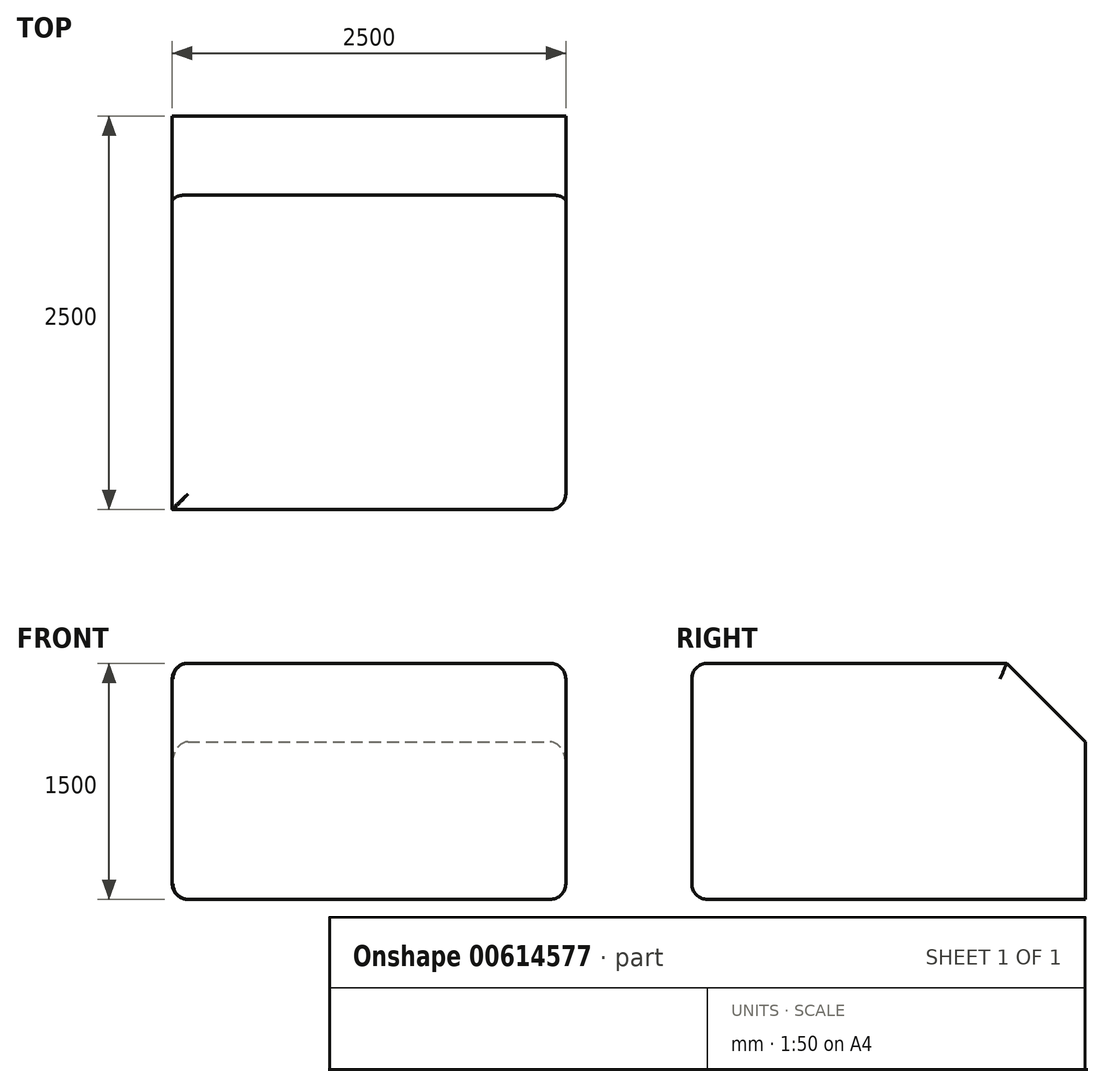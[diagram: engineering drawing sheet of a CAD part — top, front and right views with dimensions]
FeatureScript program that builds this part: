
annotation { "Feature Type Name" : "Feature", "Feature Type Description" : "" }
export const myFeature = defineFeature(function(context is Context, id is Id, definition is map)
    precondition{}
    {
        {
            var Q0;
            Q0=qCreatedBy(makeId("Top.planeOp"),FACE);
            var sketch = newSketch(context, id + "F0", { "sketchPlane" : qUnion([Q0])});
            skLineSegment(sketch, "E0.bottom", {"start": v(1250, -1250) * mm, "end": v(-1245, -1250) * mm});
            skLineSegment(sketch, "E0.top", {"start": v(1250, 1250) * mm, "end": v(-1250, 1250) * mm});
            skLineSegment(sketch, "E0.left", {"start": v(1250, -1250) * mm, "end": v(1250, 1250) * mm});
            skLineSegment(sketch, "E0.right", {"start": v(-1250, -1245) * mm, "end": v(-1250, 1250) * mm});
            skPoint(sketch, "E0.middle", {"position": v(0, 0) * mm});
            skPoint(sketch, "E1.visualSharp", {"position": v(-1250, -1250) * mm});
            skArc(sketch, "E1.filletArc", {"start": v(-1250, -1245) * mm, "mid": v(-1248.54, -1248.54) * mm, "end": v(-1245, -1250) * mm});
            skSolve(sketch);
        }
        {
            var Q0;
            Q0 = qSketchRegion(id + "F0", true);
            var Q1;
            Q1=makeQuery(id+"F0.imprint","IMPRINT",FACE,{"disambiguationData":[TD([[makeQuery(id+"F0.imprint","IMPRINT",EDGE,{"derivedFrom":sQuery(id+"F0.wireOp",EDGE,"E0.bottom")}),-1.0]])]});
            extrude(context, id + "F1", {"entities" : qUnion([Q0, Q1]), "depth" : 1500 * mm, "offsetDistance" : 25 * mm});
        }
        {
            var Q0;
            Q0=makeQuery(id+"F1.opExtrude","CAP_EDGE",EDGE,{"disambiguationData":[OSD([sQuery(id+"F0.wireOp",EDGE,"E0.top")])],"isStart":false});
            chamfer(context, id + "F2", {"entities" : qUnion([Q0]), "width" : 500 * mm, "tangentPropagation" : true});
        }
        {
            var Q0;
            Q0=makeQuery(id+"F1.opExtrude","CAP_EDGE",EDGE,{"disambiguationData":[OSD([sQuery(id+"F0.wireOp",EDGE,"E0.right")])],"isStart":true});
            var Q1;
            Q1=makeQuery(id+"F1.opExtrude","CAP_EDGE",EDGE,{"disambiguationData":[OSD([sQuery(id+"F0.wireOp",EDGE,"E0.left")])],"isStart":true});
            var Q2;
            Q2=makeQuery(id+"F1.opExtrude","SWEPT_EDGE",EDGE,{"disambiguationData":[OSD([sQuery(id+"F0.wireOp",EDGE,"E0.right"),sQuery(id+"F0.wireOp",EDGE,"E1.filletArc")])]});
            var Q3;
            Q3=makeQuery(id+"F1.opExtrude","CAP_EDGE",EDGE,{"disambiguationData":[OSD([sQuery(id+"F0.wireOp",EDGE,"E0.bottom")])],"isStart":false});
            var Q4;
            Q4=makeQuery(id+"F1.opExtrude","SWEPT_EDGE",EDGE,{"disambiguationData":[OSD([sQuery(id+"F0.wireOp",EDGE,"E0.bottom"),sQuery(id+"F0.wireOp",EDGE,"E0.left")])]});
            var Q5;
            Q5=makeQuery(id+"F1.opExtrude","CAP_EDGE",EDGE,{"disambiguationData":[OSD([sQuery(id+"F0.wireOp",EDGE,"E0.bottom")])],"isStart":true});
            var Q6;
            Q6=makeQuery(id+"F1.opExtrude","CAP_EDGE",EDGE,{"disambiguationData":[OSD([sQuery(id+"F0.wireOp",EDGE,"E0.right")])],"isStart":false});
            var Q7;
            Q7=makeQuery(id+"F2.opChamfer","BLEND_EDGE",EDGE,{"blendedFrom":[makeQuery(id+"F1.opExtrude","CAP_EDGE",EDGE,{"disambiguationData":[OSD([sQuery(id+"F0.wireOp",EDGE,"E0.top")])],"isStart":false}),makeQuery(id+"F1.opExtrude","SWEPT_FACE",FACE,{"disambiguationData":[OSD([sQuery(id+"F0.wireOp",EDGE,"E0.right")])]})],"blendedInto":[makeQuery(id+"F1.opExtrude","SWEPT_FACE",FACE,{"disambiguationData":[OSD([sQuery(id+"F0.wireOp",EDGE,"E0.right")])]})]});
            var Q8;
            Q8=makeQuery(id+"F1.opExtrude","CAP_EDGE",EDGE,{"disambiguationData":[OSD([sQuery(id+"F0.wireOp",EDGE,"E0.left")])],"isStart":false});
            var Q9;
            Q9=makeQuery(id+"F2.opChamfer","BLEND_EDGE",EDGE,{"blendedFrom":[makeQuery(id+"F1.opExtrude","CAP_EDGE",EDGE,{"disambiguationData":[OSD([sQuery(id+"F0.wireOp",EDGE,"E0.top")])],"isStart":false}),makeQuery(id+"F1.opExtrude","SWEPT_FACE",FACE,{"disambiguationData":[OSD([sQuery(id+"F0.wireOp",EDGE,"E0.left")])]})],"blendedInto":[makeQuery(id+"F1.opExtrude","SWEPT_FACE",FACE,{"disambiguationData":[OSD([sQuery(id+"F0.wireOp",EDGE,"E0.left")])]})]});
            fillet(context, id + "F3", {"entities" : qUnion([Q0, Q1, Q2, Q3, Q4, Q5, Q6, Q7, Q8, Q9]), "radius" : 100 * mm, "tangentPropagation" : true, "allowEdgeOverflow" : false});
        }
    });
